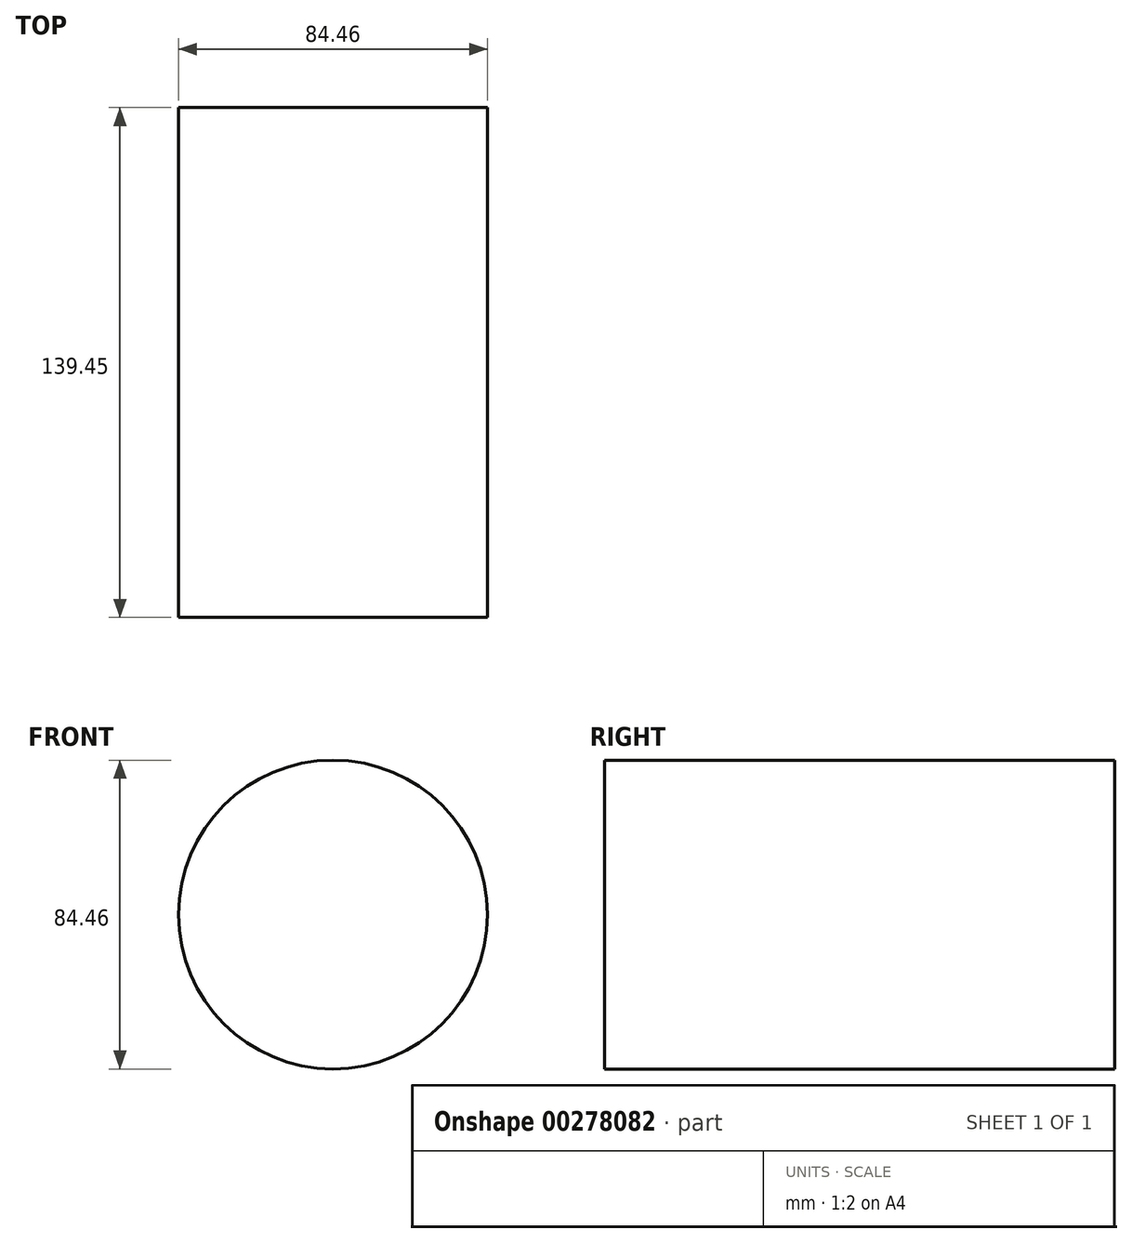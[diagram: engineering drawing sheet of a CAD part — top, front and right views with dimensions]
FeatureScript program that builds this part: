
annotation { "Feature Type Name" : "Feature", "Feature Type Description" : "" }
export const myFeature = defineFeature(function(context is Context, id is Id, definition is map)
    precondition{}
    {
        {
            var Q0;
            Q0=qCreatedBy(makeId("Front.planeOp"),FACE);
            var sketch = newSketch(context, id + "F0", { "sketchPlane" : qUnion([Q0])});
            skCircle(sketch, "E0", {"center": v(-25.25, 28.83) * mm, "radius": 42.23 * mm});
            skSolve(sketch);
        }
        {
            var Q0;
            Q0 = qSketchRegion(id + "F0", true);
            extrude(context, id + "F1", {"entities" : qUnion([Q0]), "depth" : 139.45 * mm});
        }
    });
